# Revit family: UOCP115-SS01A
name_source: partatom
category: Specialty Equipment
revit_build: Autodesk Revit 2017 (Build: 20160225_1515(x64)
units: mm (PartAtom-declared; Revit-internal decimal feet)

## family parameters
Always vertical = Yes
Cut with Voids When Loaded = No
OmniClass Number = 23.40.20.00
OmniClass Title = General Furniture and Specialties
Part Type = Normal
Room Calculation Point = No
Round Connector Dimension = Use Diameter
Shared = No
Work Plane-Based = No

## types (1)
- UOCP115-SS01A
    Amps = 4
    Description = 15" Clear Ice Machine
    Dimensions = 34 1/8"H x 14 15/16"W x 22 1/4"D
    Door Swing = Field Reversible
    Finish = Stainless Steel-Satin Brushed
    Lock = No
    Manufacturer = U-LINE
    Model = UOCP115-SS01A
    Pump = Yes
    Shipping Weight = 101 lb
    Temperature Range = 34° F - 60° F
    Type Comments = Field reversible door is shipped right-hand hinged
    URL = www.yepsketch.com
    Voltage/Hz = 115/60

## geometry (parser evidence)
native form markers: Sweep x9
no freeform markers — native parametric forms only
